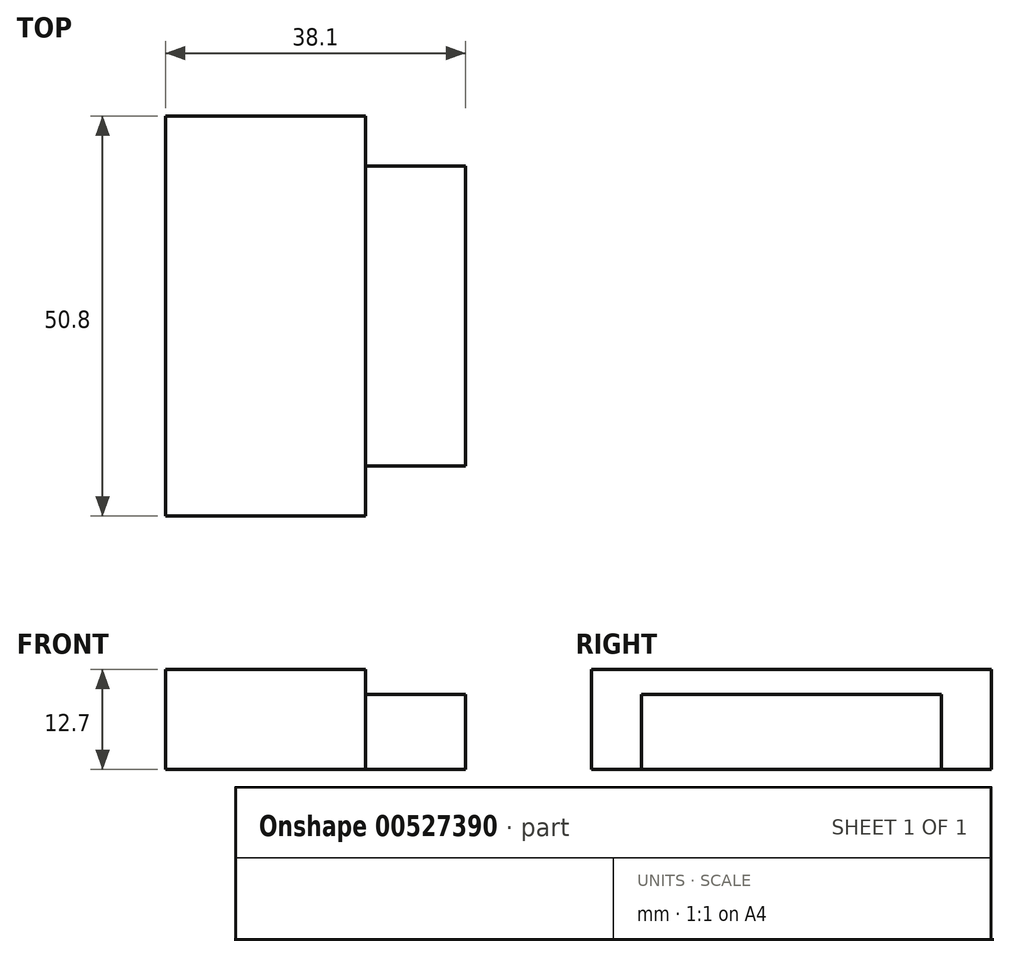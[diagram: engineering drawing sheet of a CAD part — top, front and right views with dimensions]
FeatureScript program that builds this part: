
annotation { "Feature Type Name" : "Feature", "Feature Type Description" : "" }
export const myFeature = defineFeature(function(context is Context, id is Id, definition is map)
    precondition{}
    {
        {
            var Q0;
            Q0=qCreatedBy(makeId("Top.planeOp"),FACE);
            var sketch = newSketch(context, id + "F0", { "sketchPlane" : qUnion([Q0])});
            skLineSegment(sketch, "E0.bottom", {"start": v(0, 0) * mm, "end": v(-25.4, 0) * mm});
            skLineSegment(sketch, "E0.top", {"start": v(0, 50.8) * mm, "end": v(-25.4, 50.8) * mm});
            skLineSegment(sketch, "E0.left", {"start": v(0, 0) * mm, "end": v(0, 50.8) * mm});
            skLineSegment(sketch, "E0.right", {"start": v(-25.4, 0) * mm, "end": v(-25.4, 50.8) * mm});
            skSolve(sketch);
        }
        {
            var Q0;
            Q0=makeQuery(id+"F0.imprint","IMPRINT",FACE,{"disambiguationData":[TD([[makeQuery(id+"F0.imprint","IMPRINT",EDGE,{"derivedFrom":sQuery(id+"F0.wireOp",EDGE,"E0.bottom")}),-1.0]])]});
            var Q1;
            Q1=sQuery(id+"F0.wireOp",EDGE,"E0.right");
            var Q2;
            Q2=sQuery(id+"F0.wireOp",EDGE,"E0.top");
            var Q3;
            Q3=sQuery(id+"F0.wireOp",EDGE,"E0.left");
            var Q4;
            Q4=sQuery(id+"F0.wireOp",EDGE,"E0.bottom");
            extrude(context, id + "F1", {"entities" : qUnion([Q0]), "surfaceEntities" : qUnion([Q1, Q2, Q3, Q4]), "depth" : 12.7 * mm, "offsetDistance" : 25.4 * mm});
        }
        {
            var Q0;
            Q0=makeQuery(id+"F1.opExtrude","CAP_FACE",FACE,{"disambiguationData":[OSD([sQuery(id+"F0.wireOp",EDGE,"E0.bottom"),sQuery(id+"F0.wireOp",EDGE,"E0.top"),sQuery(id+"F0.wireOp",EDGE,"E0.left"),sQuery(id+"F0.wireOp",EDGE,"E0.right")])],"isStart":true});
            var sketch = newSketch(context, id + "F2", { "sketchPlane" : qUnion([Q0])});
            skLineSegment(sketch, "E1.bottom", {"start": v(0, -6.35) * mm, "end": v(12.7, -6.35) * mm});
            skLineSegment(sketch, "E1.top", {"start": v(0, -44.45) * mm, "end": v(12.7, -44.45) * mm});
            skLineSegment(sketch, "E1.left", {"start": v(0, -6.35) * mm, "end": v(0, -44.45) * mm});
            skLineSegment(sketch, "E1.right", {"start": v(12.7, -6.35) * mm, "end": v(12.7, -44.45) * mm});
            skSolve(sketch);
        }
        {
            var Q0;
            Q0 = qSketchRegion(id + "F2", true);
            extrude(context, id + "F3", {"entities" : qUnion([Q0]), "operationType" : NewBodyOperationType.ADD, "oppositeDirection" : true, "depth" : 9.52 * mm, "offsetDistance" : 25.4 * mm});
        }
    });
